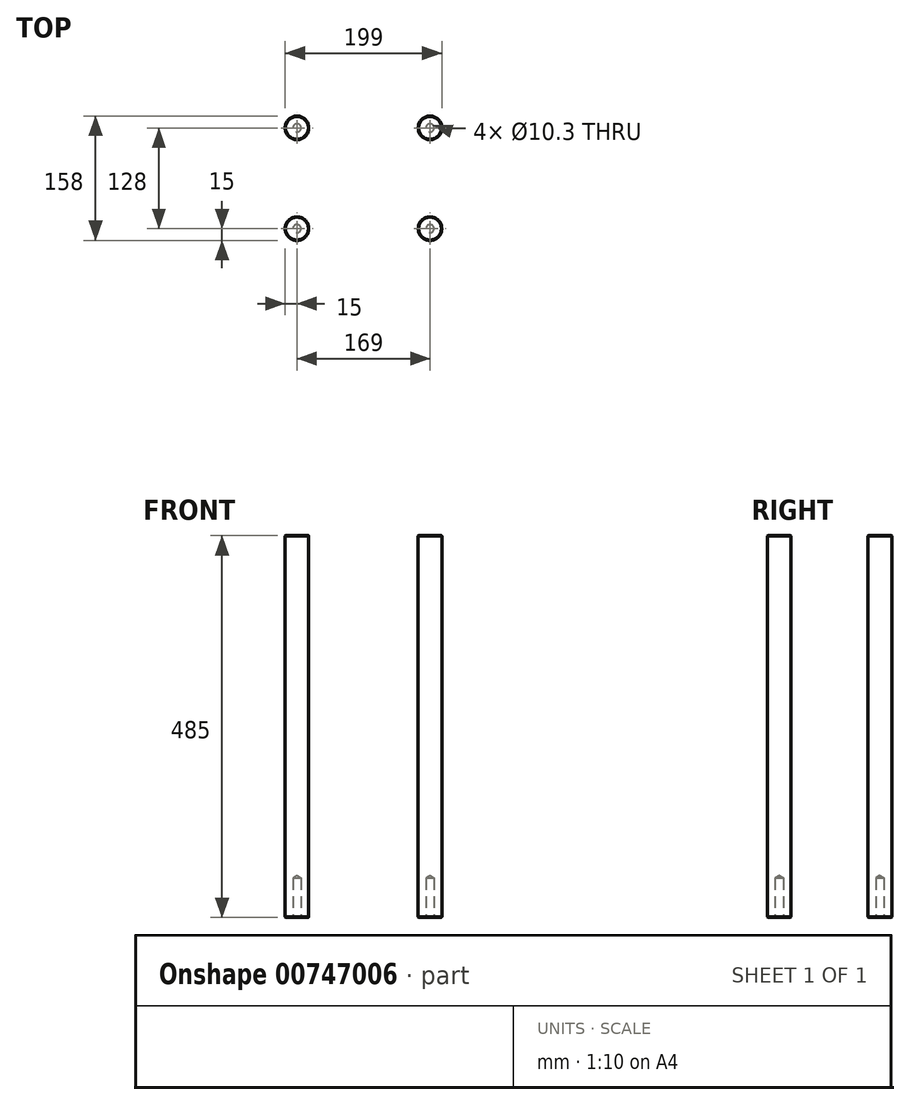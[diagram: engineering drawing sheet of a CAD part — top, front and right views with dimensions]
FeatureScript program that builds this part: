
annotation { "Feature Type Name" : "Feature", "Feature Type Description" : "" }
export const myFeature = defineFeature(function(context is Context, id is Id, definition is map)
    precondition{}
    {
        {
            var Q0;
            Q0=qCreatedBy(makeId("Top.planeOp"),FACE);
            var sketch = newSketch(context, id + "F0", { "sketchPlane" : qUnion([Q0])});
            skArc(sketch, "E0", {"start": v(76.68, 49) * mm, "mid": v(-91, 0) * mm, "end": v(76.68, -49) * mm, "construction": true});
            skLineSegment(sketch, "E1.top", {"start": v(89, -49) * mm, "end": v(89, 49) * mm, "construction": true});
            skLineSegment(sketch, "E1.left", {"start": v(76.68, -49) * mm, "end": v(89, -49) * mm, "construction": true});
            skLineSegment(sketch, "E1.right", {"start": v(76.68, 49) * mm, "end": v(89, 49) * mm, "construction": true});
            skCircle(sketch, "E2", {"center": v(84.5, -64) * mm, "radius": 15 * mm});
            skCircle(sketch, "E3", {"center": v(-84.5, -64) * mm, "radius": 15 * mm});
            skCircle(sketch, "E4", {"center": v(-84.5, 64) * mm, "radius": 15 * mm});
            skCircle(sketch, "E5", {"center": v(84.5, 64) * mm, "radius": 15 * mm});
            skSolve(sketch);
        }
        {
            var Q0;
            Q0=qSketchRegion(id+"F0",true);
            extrude(context, id + "F1", {"entities" : qUnion([Q0]), "depth" : 485 * mm, "offsetDistance" : 25 * mm});
        }
        {
            var Q0;
            Q0=sQuery(id+"F0.wireOp",VERTEX,"E4.center");
            var Q1;
            Q1=sQuery(id+"F0.wireOp",VERTEX,"E3.center");
            var Q2;
            Q2=sQuery(id+"F0.wireOp",VERTEX,"E2.center");
            var Q3;
            Q3=sQuery(id+"F0.wireOp",VERTEX,"E5.center");
            var Q4;
            Q4=makeQuery(id+"F1.opExtrude","SWEPT_BODY",BODY,{"disambiguationData":[OSD([sQuery(id+"F0.wireOp",EDGE,"E4")])]});
            var Q5;
            Q5=makeQuery(id+"F1.opExtrude","SWEPT_BODY",BODY,{"disambiguationData":[OSD([sQuery(id+"F0.wireOp",EDGE,"E3")])]});
            var Q6;
            Q6=makeQuery(id+"F1.opExtrude","SWEPT_BODY",BODY,{"disambiguationData":[OSD([sQuery(id+"F0.wireOp",EDGE,"E2")])]});
            var Q7;
            Q7=makeQuery(id+"F1.opExtrude","SWEPT_BODY",BODY,{"disambiguationData":[OSD([sQuery(id+"F0.wireOp",EDGE,"E5")])]});
            hole(context, id + "F2", {"style" : HoleStyle.SIMPLE, "endStyle" : HoleEndStyle.BLIND, "oppositeDirection" : true, "standardTappedOrClearance" : lookupTablePath({ "standard" : "ISO", "engagement" : "75%", "pitch" : "1.75 mm", "size" : "M12", "type" : "Tapped" }), "standardBlindInLast" : lookupTablePath({ "standard" : "ISO", "engagement" : "75%", "pitch" : "1.75 mm", "size" : "M12", "type" : "Tapped" }), "holeDiameter" : 10.3 * mm, "majorDiameter" : 12 * mm, "showTappedDepth" : true, "holeDepth" : 50 * mm, "isTappedThrough" : true, "tappedDepth" : 44.75 * mm, "tapClearance" : 3, "locations" : qUnion([Q0, Q1, Q2, Q3]), "scope" : qUnion([Q4, Q5, Q6, Q7])});
        }
        {
            var Q0;
            Q0=makeQuery(id+"F1.opExtrude","SWEPT_FACE",FACE,{"disambiguationData":[OSD([sQuery(id+"F0.wireOp",EDGE,"E2")])]});
            var Q1;
            Q1=makeQuery(id+"F1.opExtrude","SWEPT_FACE",FACE,{"disambiguationData":[OSD([sQuery(id+"F0.wireOp",EDGE,"E3")])]});
            var Q2;
            Q2=makeQuery(id+"F1.opExtrude","SWEPT_FACE",FACE,{"disambiguationData":[OSD([sQuery(id+"F0.wireOp",EDGE,"E5")])]});
            var Q3;
            Q3=makeQuery(id+"F1.opExtrude","SWEPT_FACE",FACE,{"disambiguationData":[OSD([sQuery(id+"F0.wireOp",EDGE,"E4")])]});
            chamfer(context, id + "F3", {"entities" : qUnion([Q0, Q1, Q2, Q3]), "width" : .5 * mm, "tangentPropagation" : true});
        }
    });
